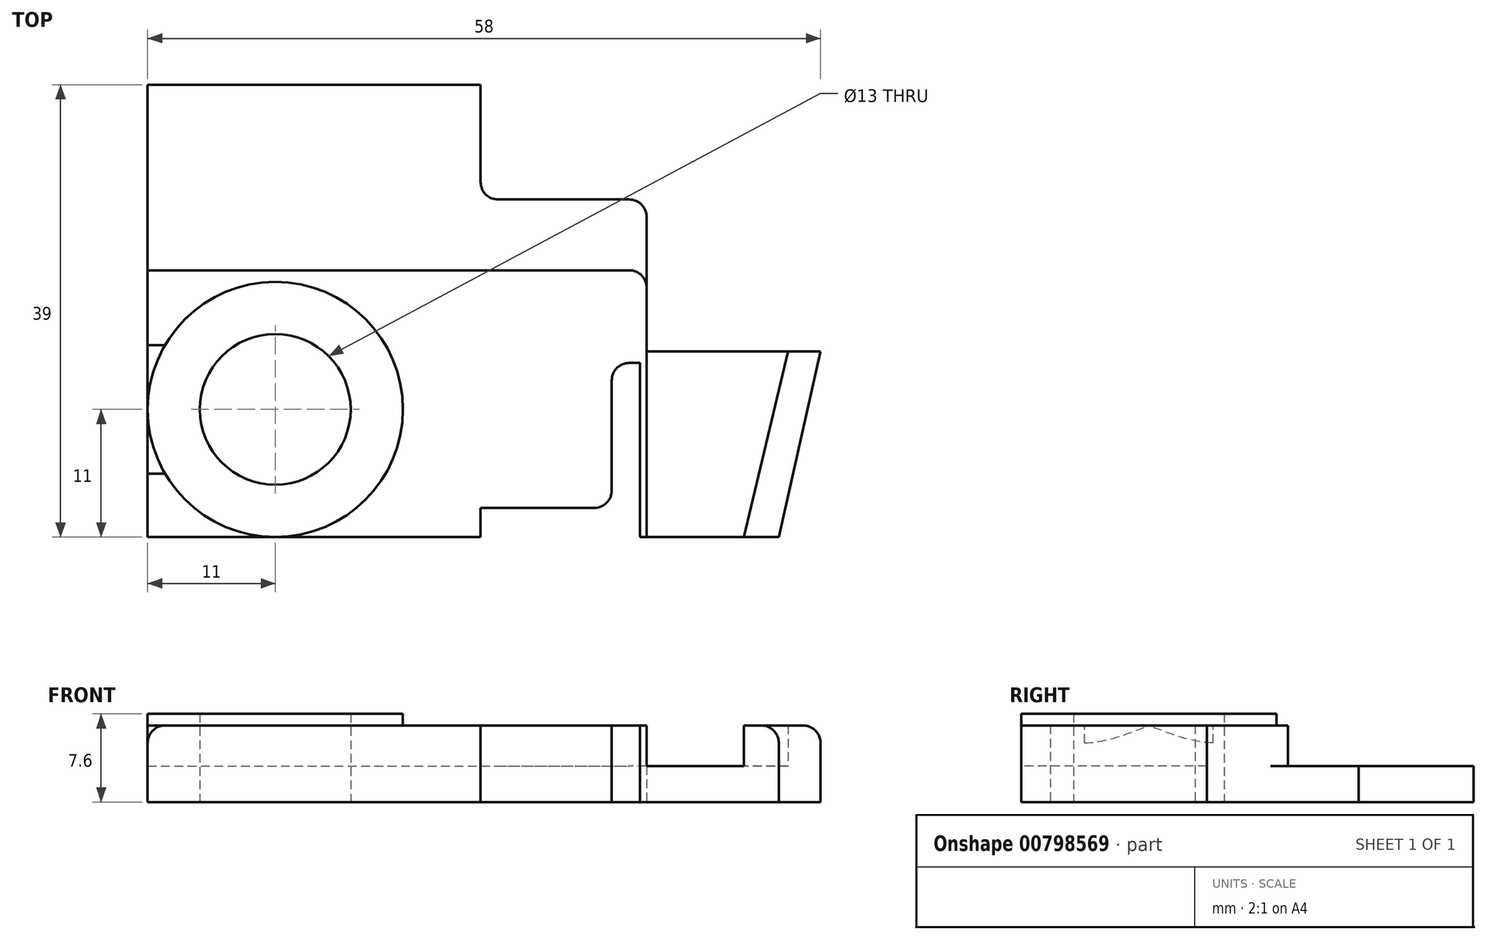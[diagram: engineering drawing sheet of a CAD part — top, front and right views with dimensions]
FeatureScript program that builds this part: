
annotation { "Feature Type Name" : "Feature", "Feature Type Description" : "" }
export const myFeature = defineFeature(function(context is Context, id is Id, definition is map)
    precondition{}
    {
        {
            var Q0;
            Q0=qCreatedBy(makeId("Top.planeOp"),FACE);
            var sketch = newSketch(context, id + "F0", { "sketchPlane" : qUnion([Q0])});
            skLineSegment(sketch, "E0.bottom", {"start": v(0, 0) * mm, "end": v(43, 0) * mm});
            skLineSegment(sketch, "E0.top", {"start": v(0, -42) * mm, "end": v(43, -42) * mm});
            skLineSegment(sketch, "E0.left", {"start": v(0, 0) * mm, "end": v(0, -42) * mm});
            skLineSegment(sketch, "E0.right", {"start": v(43, 0) * mm, "end": v(43, -42) * mm});
            skLineSegment(sketch, "E1.bottom", {"start": v(43, 0) * mm, "end": v(28.7, 0) * mm});
            skLineSegment(sketch, "E1.top", {"start": v(43, -42) * mm, "end": v(28.7, -42) * mm});
            skLineSegment(sketch, "E1.right", {"start": v(28.7, 0) * mm, "end": v(28.7, -42) * mm});
            skLineSegment(sketch, "E2.bottom", {"start": v(28.7, 0) * mm, "end": v(43, 0) * mm});
            skLineSegment(sketch, "E2.top", {"start": v(28.7, -12.9) * mm, "end": v(43, -12.9) * mm});
            skLineSegment(sketch, "E2.left", {"start": v(28.7, 0) * mm, "end": v(28.7, -12.9) * mm});
            skLineSegment(sketch, "E2.right", {"start": v(43, 0) * mm, "end": v(43, -12.9) * mm});
            skPoint(sketch, "E3", {"position": v(11, -31) * mm});
            skCircle(sketch, "E4", {"center": v(11, -31) * mm, "radius": 6.5 * mm});
            skLineSegment(sketch, "E5.bottom", {"start": v(0, 0) * mm, "end": v(28.7, 0) * mm});
            skLineSegment(sketch, "E5.top", {"start": v(0, -3) * mm, "end": v(28.7, -3) * mm});
            skLineSegment(sketch, "E5.left", {"start": v(0, 0) * mm, "end": v(0, -3) * mm});
            skLineSegment(sketch, "E5.right", {"start": v(28.7, 0) * mm, "end": v(28.7, -3) * mm});
            skLineSegment(sketch, "E6.top", {"start": v(28.7, -27) * mm, "end": v(43, -27) * mm});
            skLineSegment(sketch, "E6.left", {"start": v(28.7, -12.9) * mm, "end": v(28.7, -27) * mm});
            skLineSegment(sketch, "E6.right", {"start": v(43, -12.9) * mm, "end": v(43, -27) * mm});
            skLineSegment(sketch, "E7.bottom", {"start": v(43, -27) * mm, "end": v(42.45, -27) * mm});
            skLineSegment(sketch, "E7.top", {"start": v(43, -42) * mm, "end": v(42.45, -42) * mm});
            skLineSegment(sketch, "E7.left", {"start": v(43, -27) * mm, "end": v(43, -42) * mm});
            skLineSegment(sketch, "E7.right", {"start": v(42.45, -27) * mm, "end": v(42.45, -42) * mm});
            skLineSegment(sketch, "E8.top", {"start": v(0, -19) * mm, "end": v(28.7, -19) * mm});
            skLineSegment(sketch, "E8.left", {"start": v(0, -3) * mm, "end": v(0, -19) * mm});
            skLineSegment(sketch, "E8.right", {"start": v(28.7, -3) * mm, "end": v(28.7, -19) * mm});
            skLineSegment(sketch, "E9", {"start": v(28.7, -22) * mm, "end": v(0, -22) * mm});
            skLineSegment(sketch, "E10", {"start": v(28.7, -19) * mm, "end": v(43, -19) * mm});
            skLineSegment(sketch, "E11.bottom", {"start": v(43, -22) * mm, "end": v(40, -22) * mm});
            skLineSegment(sketch, "E11.top", {"start": v(43, -42) * mm, "end": v(40, -42) * mm});
            skLineSegment(sketch, "E11.left", {"start": v(43, -22) * mm, "end": v(43, -42) * mm});
            skLineSegment(sketch, "E11.right", {"start": v(40, -22) * mm, "end": v(40, -42) * mm});
            skPoint(sketch, "E12", {"position": v(43, -26) * mm});
            skLineSegment(sketch, "E13.bottom", {"start": v(43, -26) * mm, "end": v(58, -26) * mm});
            skLineSegment(sketch, "E13.top", {"start": v(43, -42) * mm, "end": v(58, -42) * mm});
            skLineSegment(sketch, "E13.left", {"start": v(43, -26) * mm, "end": v(43, -42) * mm});
            skLineSegment(sketch, "E13.right", {"start": v(58, -26) * mm, "end": v(58, -42) * mm});
            skPoint(sketch, "E14", {"position": v(55.2, -26) * mm});
            skPoint(sketch, "E15", {"position": v(51.4, -42) * mm});
            skLineSegment(sketch, "E16", {"start": v(55.2, -26) * mm, "end": v(51.4, -42) * mm});
            skPoint(sketch, "E17", {"position": v(54.4, -42) * mm});
            skLineSegment(sketch, "E18", {"start": v(58, -26) * mm, "end": v(54.4, -42) * mm});
            skCircle(sketch, "E19.0", {"center": v(11, -31) * mm, "radius": 11 * mm});
            skPoint(sketch, "E20", {"position": v(22, -31) * mm});
            skLineSegment(sketch, "E21", {"start": v(21.25, -35) * mm, "end": v(40, -35) * mm});
            skLineSegment(sketch, "E22", {"start": v(21.25, -27) * mm, "end": v(40, -27) * mm});
            skLineSegment(sketch, "E23", {"start": v(28.7, -22) * mm, "end": v(43, -22) * mm});
            skLineSegment(sketch, "E24", {"start": v(17.98, -39.5) * mm, "end": v(40, -39.5) * mm});
            skSolve(sketch);
        }
        {
            var Q0;
            {var subQ1=sQuery(id+"F0.wireOp",EDGE,"E5.top");Q0=makeQuery(id+"F0.imprint","IMPRINT",FACE,{"disambiguationData":[TD([[makeQuery(id+"F0.imprint","IMPRINT",EDGE,{"derivedFrom":subQ1}),-1.0]])]});}
            var Q1;
            {var subQ4=sQuery(id+"F0.wireOp",EDGE,"E16");Q1=makeQuery(id+"F0.imprint","IMPRINT",FACE,{"disambiguationData":[TD([[makeQuery(id+"F0.imprint","IMPRINT",EDGE,{"derivedFrom":subQ4}),-1.0]])]});}
            var Q2;
            {var subQ0=sQuery(id+"F0.wireOp",EDGE,"E7.bottom");Q2=makeQuery(id+"F0.imprint","IMPRINT",FACE,{"disambiguationData":[TD([[makeQuery(id+"F0.imprint","IMPRINT",EDGE,{"derivedFrom":subQ0}),1.0]])]});}
            var Q3;
            {var subQ0=sQuery(id+"F0.wireOp",EDGE,"E2.top");Q3=makeQuery(id+"F0.imprint","IMPRINT",FACE,{"disambiguationData":[TD([[makeQuery(id+"F0.imprint","IMPRINT",EDGE,{"derivedFrom":subQ0}),-1.0]])]});}
            extrude(context, id + "F1", {"entities" : qUnion([Q0, Q1, Q2, Q3]), "depth" : 3.1 * mm, "offsetDistance" : 25 * mm});
        }
        {
            var Q0;
            Q0=makeQuery(id+"F0.imprint","IMPRINT",FACE,{"disambiguationData":[TD([[makeQuery(id+"F0.imprint","IMPRINT",EDGE,{"derivedFrom":sQuery(id+"F0.wireOp",EDGE,"E5.bottom")}),-1.0]])]});
            var Q1;
            {var subQ5=sQuery(id+"F0.wireOp",EDGE,"E8.top");Q1=makeQuery(id+"F0.imprint","IMPRINT",FACE,{"disambiguationData":[TD([[makeQuery(id+"F0.imprint","IMPRINT",EDGE,{"derivedFrom":subQ5}),-1.0]])]});}
            var Q2;
            {var subQ4=sQuery(id+"F0.wireOp",EDGE,"E6.top");Q2=makeQuery(id+"F0.imprint","IMPRINT",FACE,{"disambiguationData":[TD([[makeQuery(id+"F0.imprint","IMPRINT",EDGE,{"derivedFrom":subQ4}),-1.0]])]});}
            var Q3;
            {var subQ2=sQuery(id+"F0.wireOp",EDGE,"E16");Q3=makeQuery(id+"F0.imprint","IMPRINT",FACE,{"disambiguationData":[TD([[makeQuery(id+"F0.imprint","IMPRINT",EDGE,{"derivedFrom":subQ2}),1.0]])]});}
            var Q4;
            {var subQ1=sQuery(id+"F0.wireOp",EDGE,"E6.top");Q4=makeQuery(id+"F0.imprint","IMPRINT",FACE,{"disambiguationData":[TD([[makeQuery(id+"F0.imprint","IMPRINT",EDGE,{"derivedFrom":subQ1}),1.0]])]});}
            var Q5;
            {var subQ0=sQuery(id+"F0.wireOp",EDGE,"E10");Q5=makeQuery(id+"F0.imprint","IMPRINT",FACE,{"disambiguationData":[TD([[makeQuery(id+"F0.imprint","IMPRINT",EDGE,{"derivedFrom":subQ0}),-1.0]])]});}
            var Q6;
            {var subQ3=sQuery(id+"F0.wireOp",EDGE,"E21");var subQ5=sQuery(id+"F0.wireOp",EDGE,"E11.right");var subQ7=makeQuery(id+"F0.imprint","INTERSECT",VERTEX,{"derivedFrom":[subQ5,subQ3]});Q6=makeQuery(id+"F0.imprint","IMPRINT",FACE,{"disambiguationData":[TD([[makeQuery(id+"F0.imprint","IMPRINT",EDGE,{"disambiguationData":[TD([[subQ7,1.0]])],"derivedFrom":subQ3}),1.0]])]});}
            var Q7;
            {var subQ3=sQuery(id+"F0.wireOp",EDGE,"E21");var subQ5=sQuery(id+"F0.wireOp",EDGE,"E19.0");var subQ6=makeQuery(id+"F0.imprint","INTERSECT",VERTEX,{"derivedFrom":[subQ5,subQ3]});Q7=makeQuery(id+"F0.imprint","IMPRINT",FACE,{"disambiguationData":[TD([[makeQuery(id+"F0.imprint","IMPRINT",EDGE,{"disambiguationData":[TD([[subQ6,-1.0]])],"derivedFrom":subQ5}),-1.0]])]});}
            var Q8;
            {var subQ3=sQuery(id+"F0.wireOp",EDGE,"E19.0");var subQ5=sQuery(id+"F0.wireOp",EDGE,"E24");var subQ7=makeQuery(id+"F0.imprint","INTERSECT",VERTEX,{"derivedFrom":[subQ3,subQ5]});Q8=makeQuery(id+"F0.imprint","IMPRINT",FACE,{"disambiguationData":[TD([[makeQuery(id+"F0.imprint","IMPRINT",EDGE,{"disambiguationData":[TD([[subQ7,1.0]])],"derivedFrom":subQ3}),-1.0]])]});}
            var Q9;
            {var subQ0=sQuery(id+"F0.wireOp",EDGE,"E1.top");Q9=makeQuery(id+"F0.imprint","IMPRINT",FACE,{"disambiguationData":[TD([[makeQuery(id+"F0.imprint","IMPRINT",EDGE,{"derivedFrom":subQ0}),-1.0]])]});}
            var Q10;
            Q10=makeQuery(id+"F1.opExtrude","CAP_FACE",FACE,{"disambiguationData":[OSD([sQuery(id+"F0.wireOp",EDGE,"E9"),sQuery(id+"F0.wireOp",EDGE,"E11.right"),sQuery(id+"F0.wireOp",EDGE,"E19.0"),sQuery(id+"F0.wireOp",EDGE,"E22"),sQuery(id+"F0.wireOp",EDGE,"E23")])],"isStart":false});
            var Q11;
            Q11=makeQuery(id+"F1.opExtrude","CAP_FACE",FACE,{"disambiguationData":[OSD([sQuery(id+"F0.wireOp",EDGE,"E11.right"),sQuery(id+"F0.wireOp",EDGE,"E19.0"),sQuery(id+"F0.wireOp",EDGE,"E21"),sQuery(id+"F0.wireOp",EDGE,"E24")])],"isStart":false});
            var Q12;
            {var subQ0=sQuery(id+"F0.wireOp",EDGE,"E22");var subQ5=sQuery(id+"F0.wireOp",EDGE,"E19.0");var subQ7=makeQuery(id+"F0.imprint","INTERSECT",VERTEX,{"derivedFrom":[subQ5,subQ0]});Q12=makeQuery(id+"F0.imprint","IMPRINT",FACE,{"disambiguationData":[TD([[makeQuery(id+"F0.imprint","IMPRINT",EDGE,{"disambiguationData":[TD([[subQ7,-1.0]])],"derivedFrom":subQ5}),-1.0]])]});}
            var Q13;
            {var subQ3=sQuery(id+"F0.wireOp",EDGE,"E23");var subQ5=sQuery(id+"F0.wireOp",EDGE,"E11.right");var subQ7=makeQuery(id+"F0.imprint","INTERSECT",VERTEX,{"derivedFrom":[subQ5,subQ3]});Q13=makeQuery(id+"F0.imprint","IMPRINT",FACE,{"disambiguationData":[TD([[makeQuery(id+"F0.imprint","IMPRINT",EDGE,{"disambiguationData":[TD([[subQ7,-1.0]])],"derivedFrom":subQ5}),-1.0]])]});}
            var Q14;
            {var subQ0=sQuery(id+"F0.wireOp",EDGE,"E21");var subQ1=sQuery(id+"F0.wireOp",EDGE,"E1.right");var subQ2=makeQuery(id+"F0.imprint","INTERSECT",VERTEX,{"derivedFrom":[subQ1,subQ0]});Q14=makeQuery(id+"F0.imprint","IMPRINT",FACE,{"disambiguationData":[TD([[makeQuery(id+"F0.imprint","IMPRINT",EDGE,{"disambiguationData":[TD([[subQ2,-1.0]])],"derivedFrom":subQ1}),1.0]])]});}
            var Q15;
            {var subQ0=sQuery(id+"F0.wireOp",EDGE,"E21");var subQ1=sQuery(id+"F0.wireOp",EDGE,"E1.right");var subQ2=makeQuery(id+"F0.imprint","INTERSECT",VERTEX,{"derivedFrom":[subQ1,subQ0]});Q15=makeQuery(id+"F0.imprint","IMPRINT",FACE,{"disambiguationData":[TD([[makeQuery(id+"F0.imprint","IMPRINT",EDGE,{"disambiguationData":[TD([[subQ2,-1.0]])],"derivedFrom":subQ1}),-1.0]])]});}
            var Q16;
            {var subQ0=sQuery(id+"F0.wireOp",EDGE,"E9");var subQ1=sQuery(id+"F0.wireOp",EDGE,"E0.left");var subQ2=makeQuery(id+"F0.imprint","INTERSECT",VERTEX,{"derivedFrom":[subQ1,subQ0]});Q16=makeQuery(id+"F0.imprint","IMPRINT",FACE,{"disambiguationData":[TD([[makeQuery(id+"F0.imprint","IMPRINT",EDGE,{"disambiguationData":[TD([[subQ2,-1.0]])],"derivedFrom":subQ1}),1.0]])]});}
            var Q17;
            {var subQ0=sQuery(id+"F0.wireOp",EDGE,"E0.left");var subQ1=sQuery(id+"F0.wireOp",EDGE,"E0.top");var subQ2=makeQuery(id+"F0.imprint","INTERSECT",VERTEX,{"derivedFrom":[subQ1,subQ0]});Q17=makeQuery(id+"F0.imprint","IMPRINT",FACE,{"disambiguationData":[TD([[makeQuery(id+"F0.imprint","IMPRINT",EDGE,{"disambiguationData":[TD([[subQ2,-1.0]])],"derivedFrom":subQ1}),1.0]])]});}
            extrude(context, id + "F2", {"entities" : qUnion([Q0, Q1, Q2, Q3, Q4, Q5, Q6, Q7, Q8, Q9, Q10, Q11, Q12, Q13, Q14, Q15, Q16, Q17]), "operationType" : NewBodyOperationType.ADD, "depth" : 6.6 * mm, "offsetDistance" : 25 * mm});
        }
        {
            var Q0;
            {var subQ0=sQuery(id+"F0.wireOp",EDGE,"E19.0");var subQ1=sQuery(id+"F0.wireOp",EDGE,"E9");var subQ2=makeQuery(id+"F0.imprint","INTERSECT",VERTEX,{"disambiguationData":[OD(0.0)],"derivedFrom":[subQ1,subQ0]});Q0=makeQuery(id+"F0.imprint","IMPRINT",FACE,{"disambiguationData":[TD([[makeQuery(id+"F0.imprint","IMPRINT",EDGE,{"disambiguationData":[TD([[subQ2,-1.0]])],"derivedFrom":subQ1}),-1.0]])]});}
            var Q1;
            Q1=makeQuery(id+"F0.imprint","IMPRINT",FACE,{"disambiguationData":[TD([[makeQuery(id+"F0.imprint","IMPRINT",EDGE,{"derivedFrom":sQuery(id+"F0.wireOp",EDGE,"E4")}),-1.0]])]});
            extrude(context, id + "F3", {"entities" : qUnion([Q0, Q1]), "operationType" : NewBodyOperationType.ADD, "depth" : 7.6 * mm, "offsetDistance" : 25 * mm});
        }
        {
            var Q0;
            Q0=makeQuery(id+"F2.opExtrude","CAP_EDGE",EDGE,{"disambiguationData":[OSD([sQuery(id+"F0.wireOp",EDGE,"E5.bottom")])],"isStart":false});
            var Q1;
            Q1=makeQuery(id+"F2.opExtrude","CAP_EDGE",EDGE,{"disambiguationData":[OSD([sQuery(id+"F0.wireOp",EDGE,"E18")])],"isStart":false});
            var Q2;
            {var subQ0=sQuery(id+"F0.wireOp",EDGE,"E11.right");Q2=makeQuery(id+"F3.opExtrude","CAP_EDGE",EDGE,{"disambiguationData":[OSD([subQ0]),TDD([makeQuery(id+"F0.imprint","IMPRINT",EDGE,{"disambiguationData":[TD([[makeQuery(id+"F0.imprint","INTERSECT",VERTEX,{"derivedFrom":[subQ0,sQuery(id+"F0.wireOp",EDGE,"E21")]}),1.0]])],"derivedFrom":subQ0})])],"isStart":false});}
            var Q3;
            {var subQ0=sQuery(id+"F0.wireOp",EDGE,"E11.right");Q3=makeQuery(id+"F3.opExtrude","CAP_EDGE",EDGE,{"disambiguationData":[OSD([subQ0]),TDD([makeQuery(id+"F0.imprint","IMPRINT",EDGE,{"disambiguationData":[TD([[makeQuery(id+"F0.imprint","INTERSECT",VERTEX,{"derivedFrom":[subQ0,sQuery(id+"F0.wireOp",EDGE,"E24")]}),-1.0]])],"derivedFrom":subQ0})])],"isStart":false});}
            var Q4;
            Q4=makeQuery(id+"F2.opExtrude","SWEPT_EDGE",EDGE,{"disambiguationData":[OSD([sQuery(id+"F0.wireOp",EDGE,"E6.right"),sQuery(id+"F0.wireOp",EDGE,"E10")])]});
            var Q5;
            Q5=makeQuery(id+"F1.opExtrude","SWEPT_EDGE",EDGE,{"disambiguationData":[OSD([sQuery(id+"F0.wireOp",EDGE,"E2.right"),sQuery(id+"F0.wireOp",EDGE,"E2.top"),sQuery(id+"F0.wireOp",EDGE,"E6.right")])]});
            var Q6;
            Q6=makeQuery(id+"F2.opExtrude","CAP_EDGE",EDGE,{"disambiguationData":[OSD([sQuery(id+"F0.wireOp",EDGE,"E0.left")])],"isStart":false});
            var Q7;
            Q7=makeQuery(id+"F2.opExtrude","CAP_EDGE",EDGE,{"disambiguationData":[OSD([sQuery(id+"F0.wireOp",EDGE,"E5.left")])],"isStart":false});
            var Q8;
            Q8=makeQuery(id+"F2.opExtrude","CAP_EDGE",EDGE,{"disambiguationData":[OSD([sQuery(id+"F0.wireOp",EDGE,"E5.right")])],"isStart":false});
            var Q9;
            Q9=makeQuery(id+"F2.opExtrude","SWEPT_EDGE",EDGE,{"disambiguationData":[OSD([sQuery(id+"F0.wireOp",EDGE,"E11.right"),sQuery(id+"F0.wireOp",EDGE,"E23")])]});
            var Q10;
            Q10=makeQuery(id+"F2.opExtrude","SWEPT_EDGE",EDGE,{"disambiguationData":[OSD([sQuery(id+"F0.wireOp",EDGE,"E6.top"),sQuery(id+"F0.wireOp",EDGE,"E11.right"),sQuery(id+"F0.wireOp",EDGE,"E22")])]});
            var Q11;
            Q11=makeQuery(id+"F2.opExtrude","SWEPT_EDGE",EDGE,{"disambiguationData":[OSD([sQuery(id+"F0.wireOp",EDGE,"E11.right"),sQuery(id+"F0.wireOp",EDGE,"E21")])]});
            var Q12;
            Q12=makeQuery(id+"F2.opExtrude","SWEPT_EDGE",EDGE,{"disambiguationData":[OSD([sQuery(id+"F0.wireOp",EDGE,"E11.right"),sQuery(id+"F0.wireOp",EDGE,"E24")])]});
            fillet(context, id + "F4", {"entities" : qUnion([Q0, Q1, Q2, Q3, Q4, Q5, Q6, Q7, Q8, Q9, Q10, Q11, Q12]), "radius" : 1.5 * mm, "tangentPropagation" : true, "allowEdgeOverflow" : false});
        }
    });
